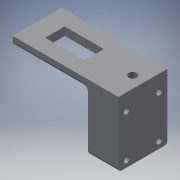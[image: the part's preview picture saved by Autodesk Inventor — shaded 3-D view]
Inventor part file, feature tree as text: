
AUTODESK INVENTOR PART (.ipt)
format: ipt  version: 2018 (Build 220112000, 112)  size: 158,720 bytes
history: native  units: mm
features: sketch x5, extrude x4, other x4, fillet x1, reference x1
ambient origin geometry x8: Origin, YZ Plane, XZ Plane, XY Plane, X Axis, Y Axis, Z Axis, Center Point
bodies: Volumenkörper1 (feature_tree)
feature tree (15):
  sketch  "Skizze1"  dims[d0=5.0mm d1=15.0mm]
  extrude  "Extrusion1"  Depth=15.0mm
  extrude  "Extrusion2"  Depth=30.0mm TaperAngle=0.0deg
  sketch  "Skizze3"  dims[d5=65.0mm d6=30.0mm]
  extrude  "Extrusion3"  Depth=30.0mm
  sketch  "Skizze4"  dims[d7=24.0mm d8=12.0mm d9=9.0mm]
  extrude  "Extrusion4"  Depth=12.0mm
  fillet  "Rundung1"  Radius=9.0mm
  sketch  "Skizze2"  dims[d2=40.0mm d3=30.0mm d4=0.0mm]
  sketch  "Skizze5"  dims[d10=5.0mm d11=0.0mm d12=3.4mm d13=3.4mm d14=3.4mm d15=3.4mm d16=10.0mm d17=20.0mm d18=5.0mm d19=10.0mm d20=4.0mm d21=20.0mm d22=4.0mm d23=5.0mm d24=20.0mm d25=0.0mm d26=5.0mm d27=10.0mm d28=0.0mm d29=2.0mm]
  reference  "Referenz1"
  other  "<userpath>\OneDrive\Development\Mohne\03_Konstruktion\StirnradUNDServo.iam"
  other  "StirnradUNDServo.iam"
  other  "Stirnräder:1"
  other  "Stirnzahnrad1:1"
